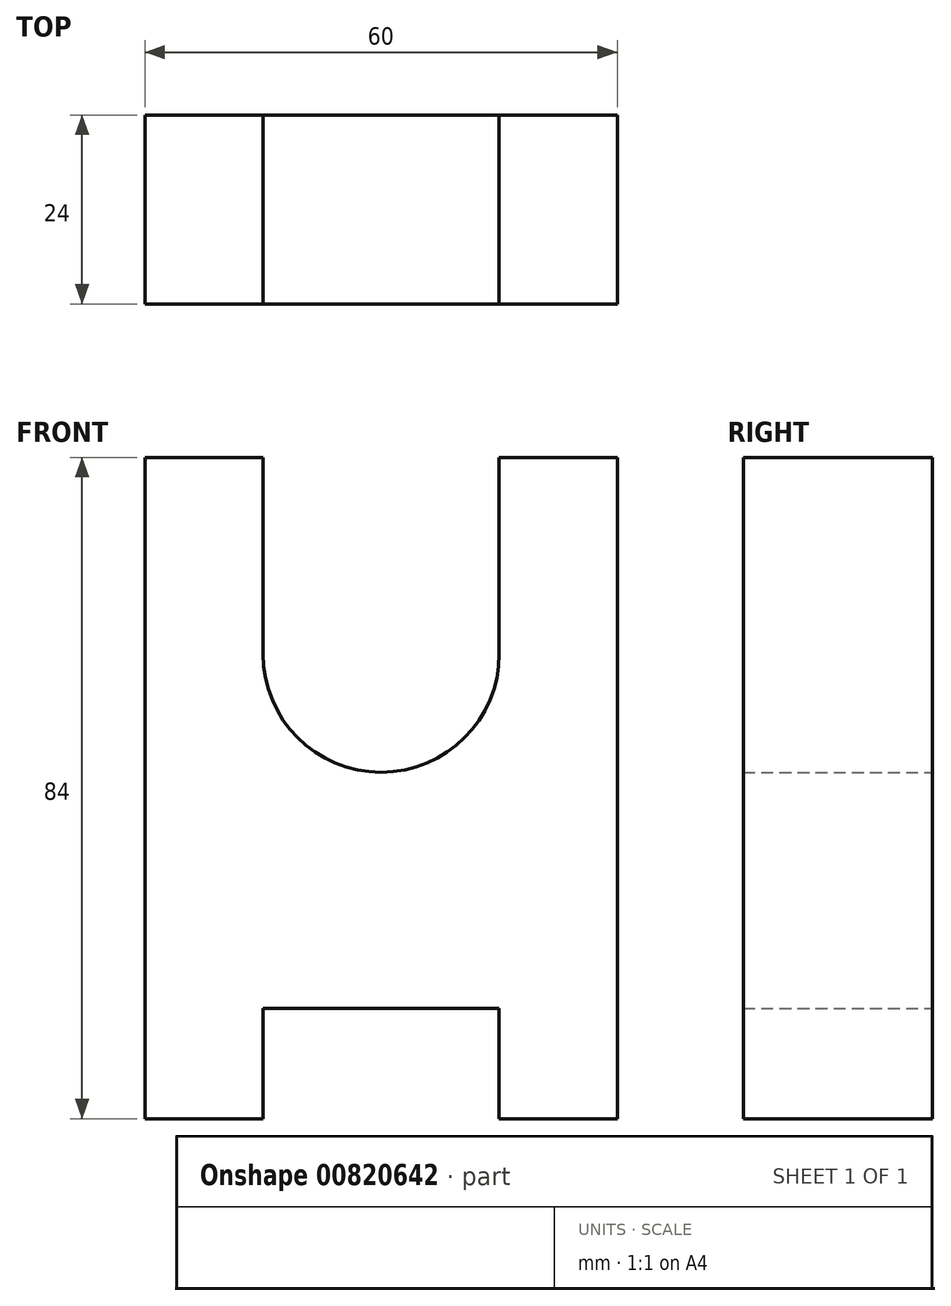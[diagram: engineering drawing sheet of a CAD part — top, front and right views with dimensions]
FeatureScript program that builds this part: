
annotation { "Feature Type Name" : "Feature", "Feature Type Description" : "" }
export const myFeature = defineFeature(function(context is Context, id is Id, definition is map)
    precondition{}
    {
        {
            var Q0;
            Q0=qCreatedBy(makeId("Front.planeOp"),FACE);
            var sketch = newSketch(context, id + "F0", { "sketchPlane" : qUnion([Q0])});
            skCircle(sketch, "E0", {"center": v(0, 0) * mm, "radius": 7.5 * mm});
            skLineSegment(sketch, "E1.bottom", {"start": v(-30, -45) * mm, "end": v(30, -45) * mm});
            skLineSegment(sketch, "E1.top", {"start": v(-30, 25) * mm, "end": v(30, 25) * mm});
            skLineSegment(sketch, "E1.left", {"start": v(-30, -45) * mm, "end": v(-30, 25) * mm});
            skLineSegment(sketch, "E1.right", {"start": v(30, -45) * mm, "end": v(30, 25) * mm});
            skPoint(sketch, "E1.middle", {"position": v(0, -10) * mm});
            skLineSegment(sketch, "E2", {"start": v(30, 25) * mm, "end": v(15, 25) * mm});
            skLineSegment(sketch, "E3", {"start": v(-30, 25) * mm, "end": v(-15, 25) * mm});
            skLineSegment(sketch, "E4", {"start": v(15, 25) * mm, "end": v(15, 0) * mm});
            skLineSegment(sketch, "E5", {"start": v(-15, 25) * mm, "end": v(-15, 0) * mm});
            skArc(sketch, "E6", {"start": v(-15, 0) * mm, "mid": v(0, -15) * mm, "end": v(15, 0) * mm});
            skLineSegment(sketch, "E7.bottom", {"start": v(30, -45) * mm, "end": v(15, -45) * mm});
            skLineSegment(sketch, "E7.top", {"start": v(30, -59) * mm, "end": v(15, -59) * mm});
            skLineSegment(sketch, "E7.left", {"start": v(30, -45) * mm, "end": v(30, -59) * mm});
            skLineSegment(sketch, "E7.right", {"start": v(15, -45) * mm, "end": v(15, -59) * mm});
            skLineSegment(sketch, "E8.bottom", {"start": v(-30, -45) * mm, "end": v(-15, -45) * mm});
            skLineSegment(sketch, "E8.top", {"start": v(-30, -59) * mm, "end": v(-15, -59) * mm});
            skLineSegment(sketch, "E8.left", {"start": v(-30, -45) * mm, "end": v(-30, -59) * mm});
            skLineSegment(sketch, "E8.right", {"start": v(-15, -45) * mm, "end": v(-15, -59) * mm});
            skLineSegment(sketch, "E9", {"start": v(15, -59) * mm, "end": v(-15, -59) * mm});
            skSolve(sketch);
        }
        {
            var Q0;
            {var subQ5=sQuery(id+"F0.wireOp",EDGE,"E1.left");Q0=makeQuery(id+"F0.imprint","IMPRINT",FACE,{"disambiguationData":[TD([[makeQuery(id+"F0.imprint","IMPRINT",EDGE,{"derivedFrom":subQ5}),-1.0]])]});}
            var Q1;
            Q1=makeQuery(id+"F0.imprint","IMPRINT",FACE,{"disambiguationData":[TD([[makeQuery(id+"F0.imprint","IMPRINT",EDGE,{"derivedFrom":sQuery(id+"F0.wireOp",EDGE,"E7.top")}),-1.0]])]});
            var Q2;
            Q2=makeQuery(id+"F0.imprint","IMPRINT",FACE,{"disambiguationData":[TD([[makeQuery(id+"F0.imprint","IMPRINT",EDGE,{"derivedFrom":sQuery(id+"F0.wireOp",EDGE,"E8.top")}),1.0]])]});
            extrude(context, id + "F1", {"entities" : qUnion([Q0, Q1, Q2]), "depth" : 24 * mm, "offsetDistance" : 25 * mm});
        }
    });
